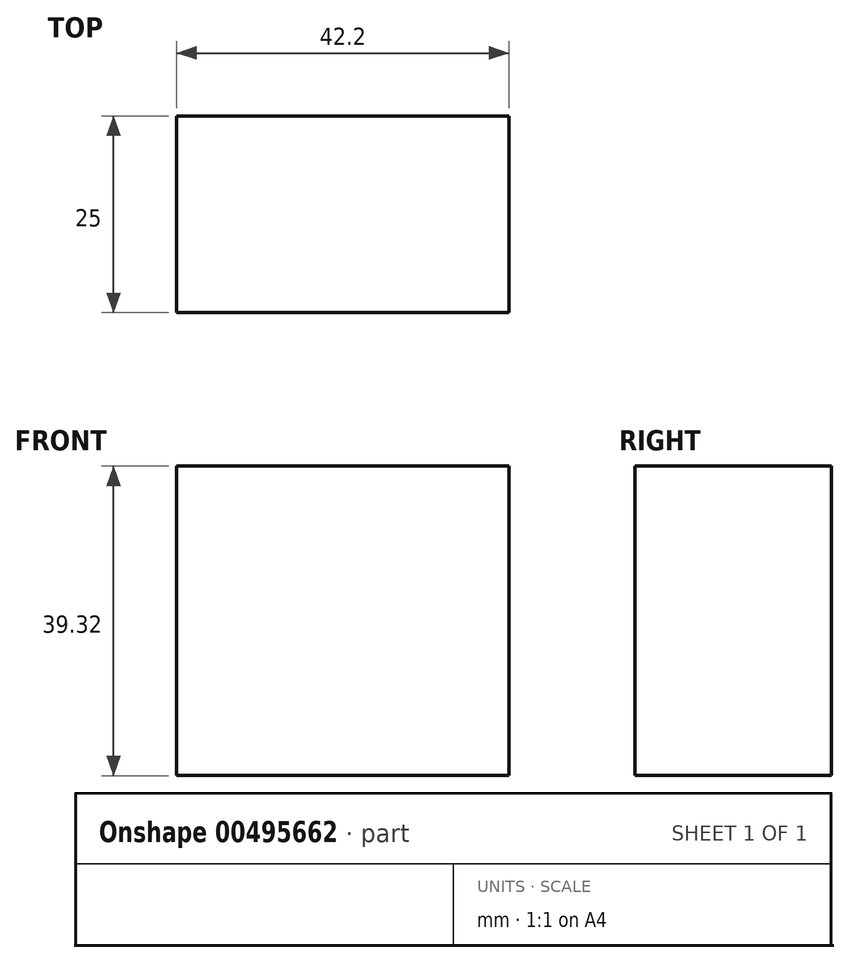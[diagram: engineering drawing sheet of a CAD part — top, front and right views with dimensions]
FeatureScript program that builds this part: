
annotation { "Feature Type Name" : "Feature", "Feature Type Description" : "" }
export const myFeature = defineFeature(function(context is Context, id is Id, definition is map)
    precondition{}
    {
        {
            var Q0;
            Q0=qCreatedBy(makeId("Front.planeOp"),FACE);
            var sketch = newSketch(context, id + "F0", { "sketchPlane" : qUnion([Q0])});
            skLineSegment(sketch, "E0.bottom", {"start": v(-21.1, -19.66) * mm, "end": v(21.1, -19.66) * mm});
            skLineSegment(sketch, "E0.top", {"start": v(-21.1, 19.66) * mm, "end": v(21.1, 19.66) * mm});
            skLineSegment(sketch, "E0.left", {"start": v(-21.1, -19.66) * mm, "end": v(-21.1, 19.66) * mm});
            skLineSegment(sketch, "E0.right", {"start": v(21.1, -19.66) * mm, "end": v(21.1, 19.66) * mm});
            skPoint(sketch, "E0.middle", {"position": v(0, 0) * mm});
            skSolve(sketch);
        }
        {
            var Q0;
            Q0=makeQuery(id+"F0.imprint","IMPRINT",FACE,{"disambiguationData":[TD([[makeQuery(id+"F0.imprint","IMPRINT",EDGE,{"derivedFrom":sQuery(id+"F0.wireOp",EDGE,"E0.bottom")}),1.0]])]});
            extrude(context, id + "F1", {"entities" : qUnion([Q0]), "depth" : 25 * mm});
        }
    });
